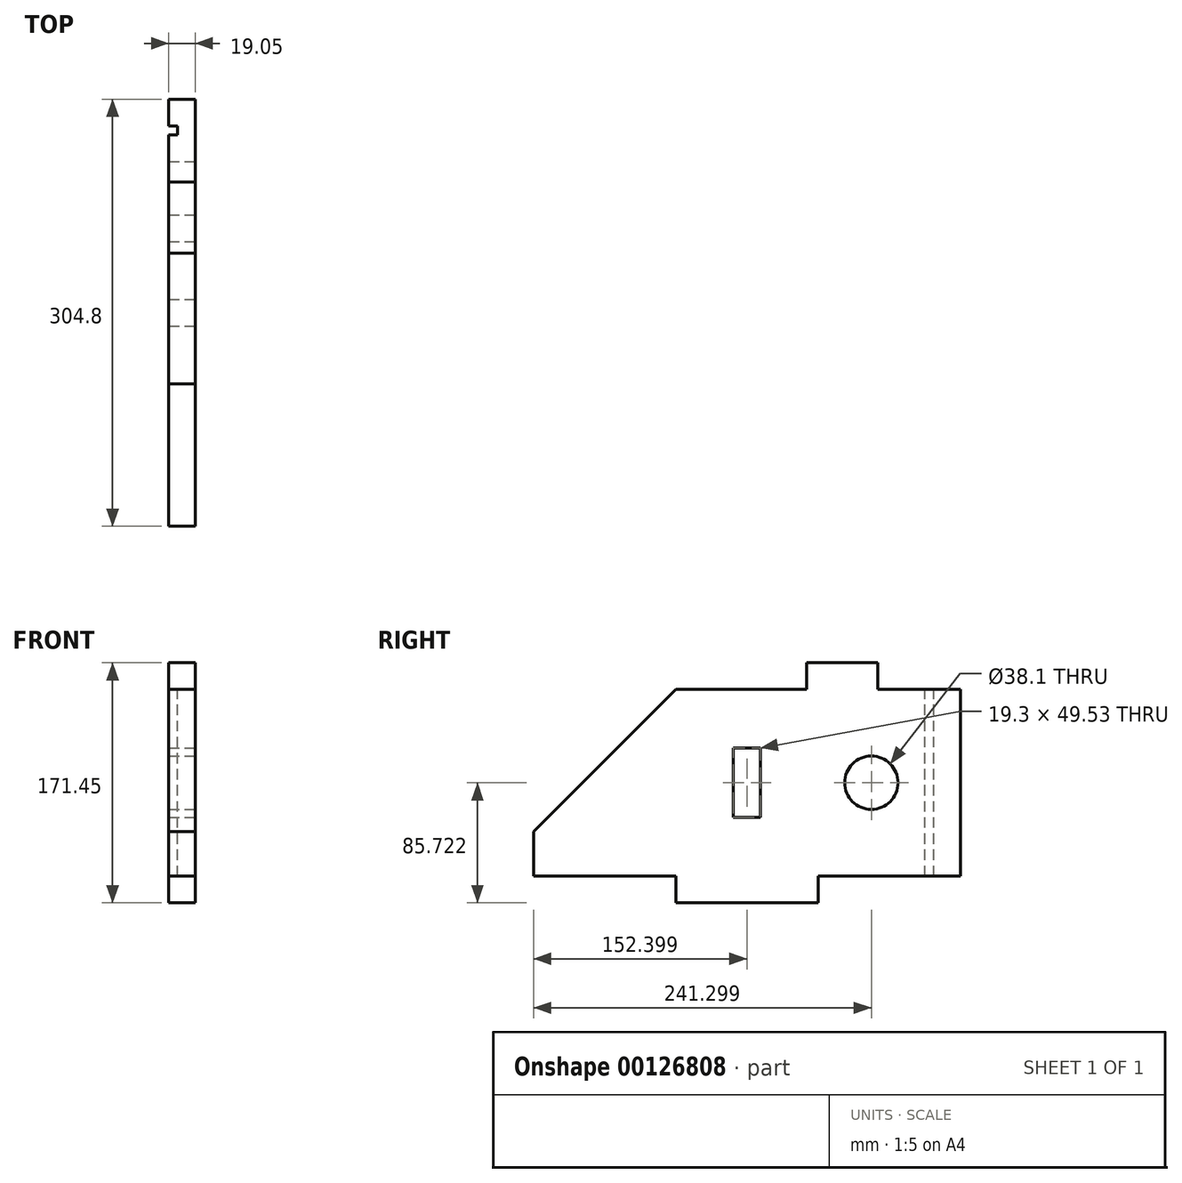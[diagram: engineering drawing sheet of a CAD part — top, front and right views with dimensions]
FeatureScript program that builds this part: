
annotation { "Feature Type Name" : "Feature", "Feature Type Description" : "" }
export const myFeature = defineFeature(function(context is Context, id is Id, definition is map)
    precondition{}
    {
        {
            var Q0;
            Q0=qCreatedBy(makeId("Right.planeOp"),FACE);
            var sketch = newSketch(context, id + "F0", { "sketchPlane" : qUnion([Q0])});
            skLineSegment(sketch, "E0.bottom", {"start": v(-248.57, -19.5) * mm, "end": v(56.23, -19.5) * mm});
            skLineSegment(sketch, "E0.top", {"start": v(-248.57, -171.9) * mm, "end": v(56.23, -171.9) * mm});
            skLineSegment(sketch, "E0.left", {"start": v(-248.57, -19.5) * mm, "end": v(-248.57, -171.9) * mm});
            skLineSegment(sketch, "E0.right", {"start": v(56.23, -19.5) * mm, "end": v(56.23, -171.9) * mm});
            skSolve(sketch);
        }
        {
            var Q0;
            Q0 = qSketchRegion(id + "F0", true);
            extrude(context, id + "F1", {"entities" : qUnion([Q0]), "depth" : 19.05 * mm});
        }
        {
            var Q0;
            Q0=makeQuery(id+"F1.opExtrude","CAP_FACE",FACE,{"disambiguationData":[OSD([sQuery(id+"F0.wireOp",EDGE,"E0.bottom"),sQuery(id+"F0.wireOp",EDGE,"E0.top"),sQuery(id+"F0.wireOp",EDGE,"E0.left"),sQuery(id+"F0.wireOp",EDGE,"E0.right")])],"isStart":false});
            var sketch = newSketch(context, id + "F2", { "sketchPlane" : qUnion([Q0])});
            skLineSegment(sketch, "E1.bottom", {"start": v(-248.57, -171.9) * mm, "end": v(-146.97, -171.9) * mm});
            skLineSegment(sketch, "E1.top", {"start": v(-248.57, -152.85) * mm, "end": v(-146.97, -152.85) * mm});
            skLineSegment(sketch, "E1.left", {"start": v(-248.57, -171.9) * mm, "end": v(-248.57, -152.85) * mm});
            skLineSegment(sketch, "E1.right", {"start": v(-146.97, -171.9) * mm, "end": v(-146.97, -152.85) * mm});
            skLineSegment(sketch, "E2.bottom", {"start": v(56.23, -171.9) * mm, "end": v(-45.37, -171.9) * mm});
            skLineSegment(sketch, "E2.top", {"start": v(56.23, -152.85) * mm, "end": v(-45.37, -152.85) * mm});
            skLineSegment(sketch, "E2.left", {"start": v(56.23, -171.9) * mm, "end": v(56.23, -152.85) * mm});
            skLineSegment(sketch, "E2.right", {"start": v(-45.37, -171.9) * mm, "end": v(-45.37, -152.85) * mm});
            skLineSegment(sketch, "E3", {"start": v(-146.97, -171.9) * mm, "end": v(-45.37, -171.9) * mm});
            skSolve(sketch);
        }
        {
            var Q0;
            Q0 = qSketchRegion(id + "F2", true);
            extrude(context, id + "F3", {"entities" : qUnion([Q0]), "operationType" : NewBodyOperationType.REMOVE, "endBound" : BoundingType.THROUGH_ALL, "oppositeDirection" : true, "depth" : 25.4 * mm});
        }
        {
            var Q0;
            Q0=makeQuery(id+"F1.opExtrude","CAP_FACE",FACE,{"disambiguationData":[OSD([sQuery(id+"F0.wireOp",EDGE,"E0.bottom"),sQuery(id+"F0.wireOp",EDGE,"E0.top"),sQuery(id+"F0.wireOp",EDGE,"E0.left"),sQuery(id+"F0.wireOp",EDGE,"E0.right")])],"isStart":false});
            var sketch = newSketch(context, id + "F4", { "sketchPlane" : qUnion([Q0])});
            skLineSegment(sketch, "E4", {"start": v(-146.97, -152.85) * mm, "end": v(-45.37, -152.85) * mm});
            skLineSegment(sketch, "E5.0", {"start": v(-86.52, -110.94) * mm, "end": v(-86.52, -61.41) * mm});
            skLineSegment(sketch, "E6.0", {"start": v(-105.82, -110.94) * mm, "end": v(-105.82, -61.41) * mm});
            skLineSegment(sketch, "E7.0", {"start": v(-105.82, -61.41) * mm, "end": v(-86.52, -61.41) * mm});
            skLineSegment(sketch, "E8.0", {"start": v(-105.82, -110.94) * mm, "end": v(-86.52, -110.94) * mm});
            skSolve(sketch);
        }
        {
            var Q0;
            Q0 = qSketchRegion(id + "F4", true);
            extrude(context, id + "F5", {"entities" : qUnion([Q0]), "operationType" : NewBodyOperationType.REMOVE, "endBound" : BoundingType.THROUGH_ALL, "oppositeDirection" : true, "depth" : 25.4 * mm});
        }
        {
            var Q0;
            Q0=makeQuery(id+"F1.opExtrude","SWEPT_FACE",FACE,{"disambiguationData":[OSD([sQuery(id+"F0.wireOp",EDGE,"E0.bottom")])]});
            var sketch = newSketch(context, id + "F6", { "sketchPlane" : qUnion([Q0])});
            skLineSegment(sketch, "E9.0", {"start": v(6.35, 37.18) * mm, "end": v(0, 37.18) * mm});
            skLineSegment(sketch, "E10.0", {"start": v(6.35, 30.83) * mm, "end": v(0, 30.83) * mm});
            skLineSegment(sketch, "E11", {"start": v(0, 37.18) * mm, "end": v(0, 30.83) * mm});
            skLineSegment(sketch, "E12.0", {"start": v(6.35, 37.18) * mm, "end": v(6.35, 30.83) * mm});
            skSolve(sketch);
        }
        {
            var Q0;
            Q0 = qSketchRegion(id + "F6", true);
            extrude(context, id + "F7", {"entities" : qUnion([Q0]), "operationType" : NewBodyOperationType.REMOVE, "endBound" : BoundingType.THROUGH_ALL, "oppositeDirection" : true, "depth" : 158 * mm});
        }
        {
            var Q0;
            Q0=makeQuery(id+"F1.opExtrude","CAP_FACE",FACE,{"disambiguationData":[OSD([sQuery(id+"F0.wireOp",EDGE,"E0.bottom"),sQuery(id+"F0.wireOp",EDGE,"E0.top"),sQuery(id+"F0.wireOp",EDGE,"E0.left"),sQuery(id+"F0.wireOp",EDGE,"E0.right")])],"isStart":false});
            var sketch = newSketch(context, id + "F8", { "sketchPlane" : qUnion([Q0])});
            skLineSegment(sketch, "E13", {"start": v(-248.57, -19.5) * mm, "end": v(-146.97, -19.5) * mm});
            skLineSegment(sketch, "E14", {"start": v(-248.57, -19.5) * mm, "end": v(-248.57, -121.1) * mm});
            skLineSegment(sketch, "E15", {"start": v(-146.97, -19.5) * mm, "end": v(-248.57, -121.1) * mm});
            skLineSegment(sketch, "E16", {"start": v(-248.57, -121.1) * mm, "end": v(-248.57, -152.85) * mm});
            skSolve(sketch);
        }
        {
            var Q0;
            Q0 = qSketchRegion(id + "F8", true);
            extrude(context, id + "F9", {"entities" : qUnion([Q0]), "operationType" : NewBodyOperationType.REMOVE, "endBound" : BoundingType.THROUGH_ALL, "oppositeDirection" : true, "depth" : 25.4 * mm});
        }
        {
            var Q0;
            Q0=makeQuery(id+"F1.opExtrude","CAP_FACE",FACE,{"disambiguationData":[OSD([sQuery(id+"F0.wireOp",EDGE,"E0.bottom"),sQuery(id+"F0.wireOp",EDGE,"E0.top"),sQuery(id+"F0.wireOp",EDGE,"E0.left"),sQuery(id+"F0.wireOp",EDGE,"E0.right")])],"isStart":false});
            var sketch = newSketch(context, id + "F10", { "sketchPlane" : qUnion([Q0])});
            skCircle(sketch, "E17", {"center": v(-7.27, -86.18) * mm, "radius": 19.05 * mm});
            skLineSegment(sketch, "E18", {"start": v(56.23, -19.5) * mm, "end": v(56.23, -152.85) * mm});
            skSolve(sketch);
        }
        {
            var Q0;
            Q0 = qSketchRegion(id + "F10", true);
            extrude(context, id + "F11", {"entities" : qUnion([Q0]), "operationType" : NewBodyOperationType.REMOVE, "endBound" : BoundingType.THROUGH_ALL, "oppositeDirection" : true, "depth" : 25.4 * mm});
        }
        {
            var Q0;
            {var subQ0=sQuery(id+"F0.wireOp",EDGE,"E0.bottom");var subQ1=sQuery(id+"F0.wireOp",EDGE,"E0.top");var subQ2=sQuery(id+"F0.wireOp",EDGE,"E0.left");Q0=makeQuery(id+"F7.boolean.opBoolean","SPLIT",FACE,{"disambiguationData":[TD([makeQuery(id+"F1.opExtrude","SWEPT_FACE",FACE,{"disambiguationData":[OSD([subQ1])]})])],"derivedFrom":makeQuery(id+"F1.opExtrude","CAP_FACE",FACE,{"disambiguationData":[OSD([subQ0,subQ1,subQ2,sQuery(id+"F0.wireOp",EDGE,"E0.right")])],"isStart":true})});}
            var sketch = newSketch(context, id + "F12", { "sketchPlane" : qUnion([Q0])});
            skLineSegment(sketch, "E19", {"start": v(86.52, -19.5) * mm, "end": v(53.5, -19.5) * mm});
            skLineSegment(sketch, "E20.bottom", {"start": v(53.5, -19.5) * mm, "end": v(2.7, -19.5) * mm});
            skLineSegment(sketch, "E20.top", {"start": v(53.5, -0.45) * mm, "end": v(2.7, -0.45) * mm});
            skLineSegment(sketch, "E20.left", {"start": v(53.5, -19.5) * mm, "end": v(53.5, -0.45) * mm});
            skLineSegment(sketch, "E20.right", {"start": v(2.7, -19.5) * mm, "end": v(2.7, -0.45) * mm});
            skLineSegment(sketch, "E21", {"start": v(86.52, -19.5) * mm, "end": v(146.97, -19.5) * mm});
            skSolve(sketch);
        }
        {
            var Q0;
            Q0 = qSketchRegion(id + "F12", true);
            extrude(context, id + "F13", {"entities" : qUnion([Q0]), "operationType" : NewBodyOperationType.ADD, "oppositeDirection" : true, "depth" : 19.05 * mm});
        }
    });
